# Revit family: 6235_Lötanschluß mit Konus
name_source: partatom
category: Rohrformteile
units: mm (PartAtom-declared; Revit-internal decimal feet)

## family parameters
Arbeitsebenenbasiert = Nein
Beim Laden mit Abzugskörper schneiden = Nein
Bemaßung runder Anschluss = Durchmesser verwenden
Gemeinsam genutzt = Nein
Immer vertikal = Ja
OmniClass-Nummer = 23.65.55.14
OmniClass-Titel = Valves for Liquid Services
Teiletyp = Verbindung

## types (5) — shared parameters
Ausführung = Lötanschluss, konisch dichtend, Mutter vernickelt, Lötnippel aus Messing
Hersteller = HERZ Armaturen Ges.m.b.H.
Lötnippel = Messing CW614N, gelb
Max. Betriebsdruck = 1000000.0 Pa
Max. Betriebstemperatur = 110 °C
Medium = Heizungswasser nach ÖNORM H5195 oder VDI- Richtlinie 2035.
Die Verwendung von Ethylen- oder Propyleneglykol in einem Mischungsverhältnis 25- 50% ist zulässig.
Mutter = Messing CW614N, vernickelt
S02 = 8 mm  [stored 0.0262467 ft]
SCRNCODE = 07;01;02
SCRNSEQ = AWI;AWI_TYP="1001";2
URL = www.herz-armaturen.at
zero-valued in all types: Vorgabe-Ansicht

## per-type parameters (varying)
| type | 1x18 | 3_4x12 | 3_4x15 | 3_4x18 | 5_8x12 | Bestellnummer |
| G1 x 18mm | Ja | Nein | Nein | Nein | Nein | 1623512 |
| G3/4 x 18mm | Nein | Nein | Nein | Ja | Nein | 1623541 |
| G3/4 x 12mm | Nein | Ja | Nein | Nein | Nein | 1623521 |
| G3/4 x 15mm | Nein | Nein | Ja | Nein | Nein | 1623531 |
| G5/8 x 12mm | Nein | Nein | Nein | Nein | Ja | 1623510 |

note: [stored X ft] marks values corroborated as IEEE doubles in the binary element streams (Revit-internal decimal feet)
